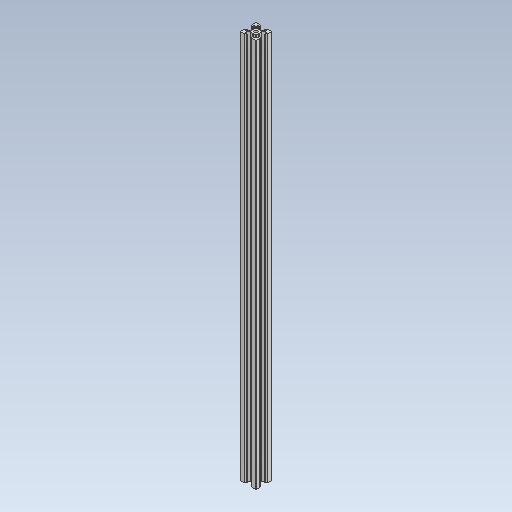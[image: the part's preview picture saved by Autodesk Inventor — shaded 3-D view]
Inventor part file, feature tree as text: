
AUTODESK INVENTOR PART (.ipt)
format: ipt  version: 2021 (Build 250183000, 183)  size: 219,648 bytes
history: native  units: mm
features: sketch x3, extrude x2, fillet x2, other x1, pattern_circular x1, hole x1, projected_geometry x1
ambient origin geometry x8: Origin, YZ Plane, XZ Plane, XY Plane, X Axis, Y Axis, Z Axis, Center Point
bodies: Body1 (feature_tree)
feature tree (11):
  other  "實體1"
  extrude  "擠出1"  Depth=20.0mm
  extrude  "擠出2"  Depth=20.0mm
  fillet  "圓角1"  Radius=500.0mm
  pattern_circular  "環形陣列1"  [2 undecoded]
  hole  "孔1"  [1 undecoded]
  fillet  "圓角2"  Radius=6.2mm
  sketch  "草圖1"
  sketch  "草圖2"
  projected_geometry  "投影迴路1"
  sketch  "草圖3"
note: 3 required parameter values undecoded (feature->parameter linkage not recoverable at this tier; creation-order binding heuristic only, values carry confidence <= 0.55)
